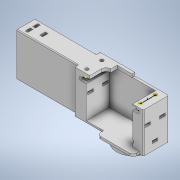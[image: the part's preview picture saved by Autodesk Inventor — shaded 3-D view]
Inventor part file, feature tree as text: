
AUTODESK INVENTOR PART (.ipt)
format: ipt  version: 2022 (Build 260153000, 153)  size: 774,656 bytes
history: native  units: mm
features: sketch x29, extrude x27, fillet x10, projected_geometry x10, other x9, mirror x1, pattern_circular x1
ambient origin geometry x8: Origin, YZ Plane, XZ Plane, XY Plane, X Axis, Y Axis, Z Axis, Center Point
bodies: Body1 (feature_tree)
feature tree (87):
  other  "Твердое тело1"
  extrude  "Выдавливание1"  Depth=29.25mm
  extrude  "Выдавливание2"  Depth=59.05mm
  extrude  "Выдавливание3"  Depth=15.0mm
  other  "РабПлоскость1"
  extrude  "Выдавливание4"  Depth=3.0mm
  other  "РабПлоскость2"
  other  "РабПлоскость3"
  other  "РабПлоскость5"
  extrude  "Выдавливание10"  Depth=41.0mm TaperAngle=0.0deg
  extrude  "Выдавливание11"  Depth=3.0mm TaperAngle=0.0deg
  fillet  "Сопряжение8"  Radius=4.2mm
  extrude  "Выдавливание12"  Depth=20.0mm TaperAngle=0.0deg
  fillet  "Сопряжение9"  [1 undecoded]
  mirror  "Зеркальное отражение2"
  extrude  "Выдавливание13"  Depth=7.15mm
  extrude  "Выдавливание15"  Depth=20.0mm
  sketch  "Эскиз18"
  other  "РабОсь1"
  extrude  "Выдавливание16"  Depth=3.25mm TaperAngle=0.0deg
  fillet  "Сопряжение12"  Radius=7.0mm
  pattern_circular  "Круговой массив1"  [2 undecoded]
  fillet  "Сопряжение14"  Radius=4.0mm
  extrude  "Выдавливание24"  Depth=1.95mm
  extrude  "Выдавливание25"  Depth=10.0mm
  extrude  "Выдавливание26"  Depth=2.0mm
  other  "РабПлоскость8"
  extrude  "Выдавливание27"  Depth=1.5mm TaperAngle=0.0deg
  extrude  "Выдавливание28"  Depth=1.0mm
  extrude  "Выдавливание29"  Depth=0.2mm
  extrude  "Выдавливание30"  Depth=19.0mm
  fillet  "Сопряжение18"  Radius=68.0mm
  fillet  "Сопряжение19"  Radius=3.5mm
  extrude  "Выдавливание31"  Depth=5.0mm
  fillet  "Сопряжение20"  Radius=4.1mm
  extrude  "Выдавливание32"  Depth=7.95mm
  sketch  "Эскиз36"
  other  "РабТочка1"
  extrude  "Выдавливание33"  Depth=28.1mm
  extrude  "Выдавливание17"  Depth=4.0mm TaperAngle=0.0deg
  fillet  "Сопряжение15"  Radius=18.75mm
  extrude  "Выдавливание18"  Depth=37.8mm
  extrude  "Выдавливание19"  Depth=2.0mm
  extrude  "Выдавливание20"  Depth=6.0mm TaperAngle=0.0deg
  extrude  "Выдавливание21"  Depth=0.5mm
  fillet  "Сопряжение16"  Radius=5.4mm
  extrude  "Выдавливание22"  Depth=0.7mm
  other  "РабПлоскость7"
  extrude  "Выдавливание23"  Depth=120.0mm TaperAngle=360.0deg
  fillet  "Сопряжение17"  Radius=1.5mm
  sketch  "Эскиз14"
  sketch  "Эскиз1"
  sketch  "Эскиз2"
  sketch  "Эскиз3"
  sketch  "Эскиз4"
  sketch  "Эскиз10"
  sketch  "Эскиз11"
  sketch  "Эскиз13"
  sketch  "Эскиз15"
  sketch  "Эскиз17"
  sketch  "Эскиз19"
  projected_geometry  "Спроецированная петля1"
  sketch  "Эскиз20"
  projected_geometry  "Спроецированная петля2"
  sketch  "Эскиз21"
  projected_geometry  "Спроецированная петля3"
  sketch  "Эскиз22"
  sketch  "Эскиз23"
  sketch  "Эскиз25"
  projected_geometry  "Спроецированная петля4"
  sketch  "Эскиз26"
  projected_geometry  "Спроецированная петля5"
  sketch  "Эскиз27"
  projected_geometry  "Спроецированная петля6"
  sketch  "Эскиз28"
  projected_geometry  "Спроецированная петля7"
  sketch  "Эскиз29"
  projected_geometry  "Спроецированная петля8"
  sketch  "Эскиз30"
  sketch  "Эскиз31"
  projected_geometry  "Спроецированная петля9"
  sketch  "Эскиз32"
  sketch  "Эскиз33"
  sketch  "Эскиз34"
  sketch  "Эскиз35"
  sketch  "Эскиз37"
  projected_geometry  "Спроецированная петля10"
note: 3 required parameter values undecoded (feature->parameter linkage not recoverable at this tier; creation-order binding heuristic only, values carry confidence <= 0.55)
